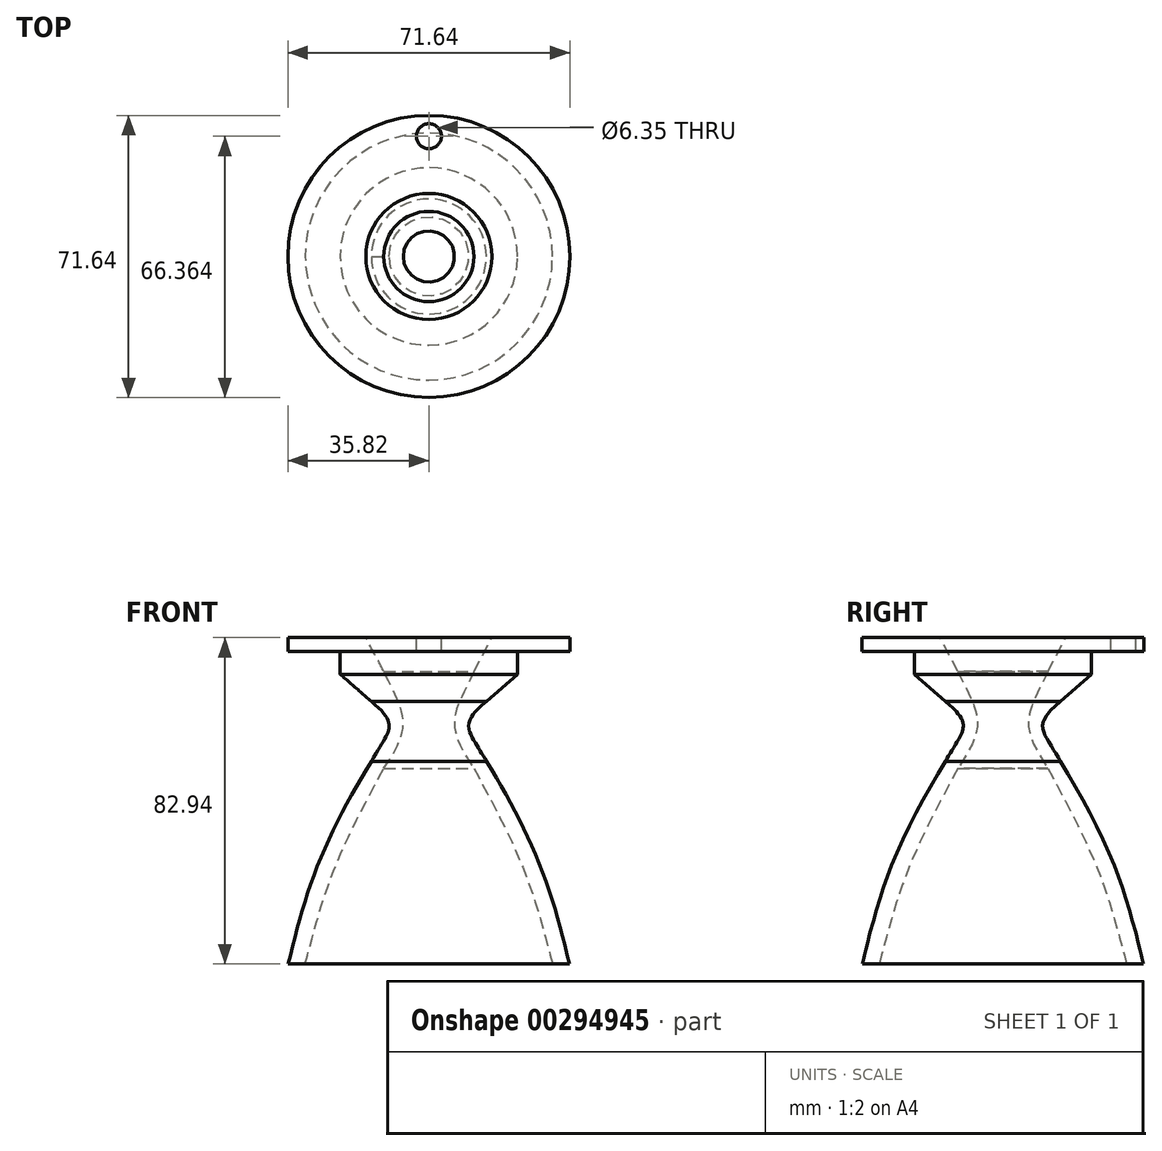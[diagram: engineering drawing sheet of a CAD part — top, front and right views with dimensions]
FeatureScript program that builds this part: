
annotation { "Feature Type Name" : "Feature", "Feature Type Description" : "" }
export const myFeature = defineFeature(function(context is Context, id is Id, definition is map)
    precondition{}
    {
        {
            var Q0;
            Q0=qCreatedBy(makeId("Front.planeOp"),FACE);
            var sketch = newSketch(context, id + "F0", { "sketchPlane" : qUnion([Q0])});
            skLineSegment(sketch, "E0", {"start": v(0, -9.82) * mm, "end": v(0, 22.74) * mm});
            skLineSegment(sketch, "E1", {"start": v(-35.71, 0) * mm, "end": v(-31.4, 0) * mm});
            skFitSpline(sketch, "E2", {"points": [v(-35.71, 0) * mm, v(-28.2, 25.17) * mm, v(-14.61, 51.47) * mm], "startDerivative": vector(12.45, 51.8) * mm, "endDerivative": vector(29.31, 47.08) * mm});
            skFitSpline(sketch, "E3", {"points": [v(-14.61, 51.47) * mm, v(-10.13, 59.83) * mm, v(-14.61, 66.69) * mm], "startDerivative": vector(13.99, 25.1) * mm, "endDerivative": vector(-24.2, 19.84) * mm});
            skFitSpline(sketch, "E4", {"points": [v(-31.4, 0) * mm, v(-24.15, 23.8) * mm, v(-11.46, 49.67) * mm], "startDerivative": vector(12.77, 49.3) * mm, "endDerivative": vector(26.93, 50.03) * mm});
            skFitSpline(sketch, "E5", {"points": [v(-11.46, 49.67) * mm, v(-6.5, 61.08) * mm, v(-11.46, 74.33) * mm], "startDerivative": vector(13.93, 20.37) * mm, "endDerivative": vector(-13.13, 28.71) * mm});
            skLineSegment(sketch, "E6", {"start": v(-11.46, 74.33) * mm, "end": v(-16.02, 82.94) * mm});
            skLineSegment(sketch, "E7", {"start": v(-16.02, 82.94) * mm, "end": v(-35.82, 82.94) * mm});
            skLineSegment(sketch, "E8", {"start": v(-35.82, 82.94) * mm, "end": v(-35.82, 79.41) * mm});
            skLineSegment(sketch, "E9", {"start": v(-35.82, 79.41) * mm, "end": v(-22.53, 79.41) * mm});
            skLineSegment(sketch, "E10", {"start": v(-22.53, 79.41) * mm, "end": v(-22.53, 73.62) * mm});
            skLineSegment(sketch, "E11", {"start": v(-22.53, 73.62) * mm, "end": v(-14.61, 66.69) * mm});
            skSolve(sketch);
        }
        {
            var Q0;
            Q0=makeQuery(id+"F0.imprint","IMPRINT",FACE,{"disambiguationData":[TD([[makeQuery(id+"F0.imprint","IMPRINT",EDGE,{"derivedFrom":sQuery(id+"F0.wireOp",EDGE,"E1")}),1.0]])]});
            var Q1;
            Q1=sQuery(id+"F0.wireOp",EDGE,"E0");
            revolve(context, id + "F1", {"entities" : qUnion([Q0]), "axis" : qUnion([Q1]), "revolveType" : RevolveType.FULL});
        }
        {
            var Q0;
            Q0=makeQuery(id+"F1.opRevolve","SWEPT_FACE",FACE,{"disambiguationData":[OSD([sQuery(id+"F0.wireOp",EDGE,"E7")])]});
            var sketch = newSketch(context, id + "F2", { "sketchPlane" : qUnion([Q0])});
            skSolve(sketch);
        }
        {
            var Q0;
            {var subQ0=sQuery(id+"F0.wireOp",EDGE,"E7");Q0=makeQuery(id+"F2.imprint","IMPRINT",FACE,{"disambiguationData":[TD([[makeQuery(id+"F2.imprint","IMPRINT",EDGE,{"derivedFrom":makeQuery(id+"F1.opRevolve","SWEPT_EDGE",EDGE,{"disambiguationData":[OSD([sQuery(id+"F0.wireOp",EDGE,"E6"),subQ0])]})}),1.0]])]});}
            var sketch = newSketch(context, id + "F3", { "sketchPlane" : qUnion([Q0])});
            skCircle(sketch, "E12", {"center": v(0, 30.54) * mm, "radius": 2.5 * mm});
            skSolve(sketch);
        }
        {
            var Q0;
            Q0=sQuery(id+"F3.wireOp",VERTEX,"E12.center");
            var Q1;
            Q1=makeQuery(id+"F1.opRevolve","SWEPT_BODY",BODY,{"disambiguationData":[OSD([sQuery(id+"F0.wireOp",EDGE,"E1"),sQuery(id+"F0.wireOp",EDGE,"E2"),sQuery(id+"F0.wireOp",EDGE,"E3"),sQuery(id+"F0.wireOp",EDGE,"E4"),sQuery(id+"F0.wireOp",EDGE,"E5"),sQuery(id+"F0.wireOp",EDGE,"E6"),sQuery(id+"F0.wireOp",EDGE,"E7"),sQuery(id+"F0.wireOp",EDGE,"E8"),sQuery(id+"F0.wireOp",EDGE,"E9"),sQuery(id+"F0.wireOp",EDGE,"E10"),sQuery(id+"F0.wireOp",EDGE,"E11")])]});
            hole(context, id + "F4", {"style" : HoleStyle.SIMPLE, "endStyle" : HoleEndStyle.BLIND, "holeDiameter" : 6.35 * mm, "holeDepth" : 12.7 * mm, "tappedDepth" : 12.7 * mm, "tapClearance" : 3, "locations" : qUnion([Q0]), "scope" : qUnion([Q1])});
        }
    });
